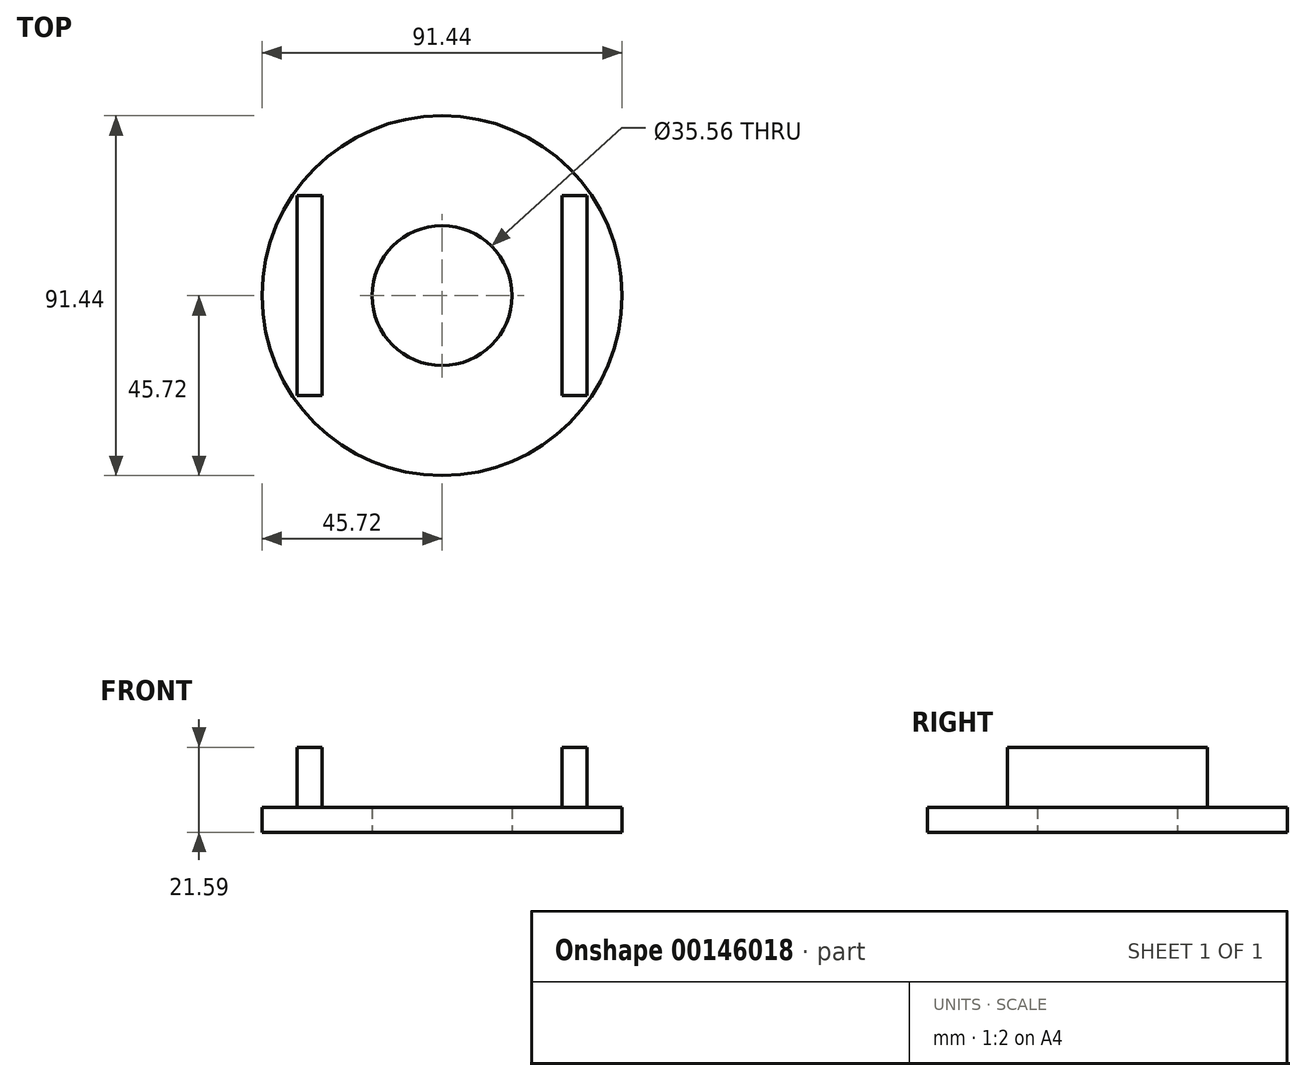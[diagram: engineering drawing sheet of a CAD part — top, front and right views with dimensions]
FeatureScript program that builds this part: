
annotation { "Feature Type Name" : "Feature", "Feature Type Description" : "" }
export const myFeature = defineFeature(function(context is Context, id is Id, definition is map)
    precondition{}
    {
        {
            var Q0;
            Q0=qCreatedBy(makeId("Top.planeOp"),FACE);
            var sketch = newSketch(context, id + "F0", { "sketchPlane" : qUnion([Q0])});
            skCircle(sketch, "E0", {"center": v(0, 0) * mm, "radius": 45.72 * mm});
            skCircle(sketch, "E1", {"center": v(0, 0) * mm, "radius": 17.78 * mm});
            skSolve(sketch);
        }
        {
            var Q0;
            Q0 = qSketchRegion(id + "F0", true);
            extrude(context, id + "F1", {"entities" : qUnion([Q0]), "depth" : 6.35 * mm, "offsetDistance" : 25.4 * mm});
        }
        {
            var Q0;
            Q0=makeQuery(id+"F1.opExtrude","CAP_FACE",FACE,{"disambiguationData":[OSD([sQuery(id+"F0.wireOp",EDGE,"E0"),sQuery(id+"F0.wireOp",EDGE,"E1")])],"isStart":false});
            var sketch = newSketch(context, id + "F2", { "sketchPlane" : qUnion([Q0])});
            skLineSegment(sketch, "E2.bottom", {"start": v(36.83, 25.4) * mm, "end": v(30.48, 25.4) * mm});
            skLineSegment(sketch, "E2.top", {"start": v(36.83, -25.4) * mm, "end": v(30.48, -25.4) * mm});
            skLineSegment(sketch, "E2.left", {"start": v(36.83, 25.4) * mm, "end": v(36.83, -25.4) * mm});
            skLineSegment(sketch, "E2.right", {"start": v(30.48, 25.4) * mm, "end": v(30.48, -25.4) * mm});
            skPoint(sketch, "E2.middle", {"position": v(33.66, 0) * mm});
            skLineSegment(sketch, "E3.MirrorCS", {"start": v(-30.48, 25.4) * mm, "end": v(-30.48, -25.4) * mm});
            skLineSegment(sketch, "E4.MirrorCS", {"start": v(-36.83, 25.4) * mm, "end": v(-30.48, 25.4) * mm});
            skLineSegment(sketch, "E5.MirrorCS", {"start": v(-36.83, 25.4) * mm, "end": v(-36.83, -25.4) * mm});
            skLineSegment(sketch, "E6.MirrorCS", {"start": v(-36.83, -25.4) * mm, "end": v(-30.48, -25.4) * mm});
            skSolve(sketch);
        }
        {
            var Q0;
            Q0=makeQuery(id+"F2.imprint","IMPRINT",FACE,{"disambiguationData":[TD([[makeQuery(id+"F2.imprint","IMPRINT",EDGE,{"derivedFrom":sQuery(id+"F2.wireOp",EDGE,"E3.MirrorCS")}),-1.0]])]});
            var Q1;
            Q1=makeQuery(id+"F2.imprint","IMPRINT",FACE,{"disambiguationData":[TD([[makeQuery(id+"F2.imprint","IMPRINT",EDGE,{"derivedFrom":sQuery(id+"F2.wireOp",EDGE,"E2.bottom")}),1.0]])]});
            extrude(context, id + "F3", {"entities" : qUnion([Q0, Q1]), "operationType" : NewBodyOperationType.ADD, "depth" : 15.24 * mm, "offsetDistance" : 25.4 * mm});
        }
    });
